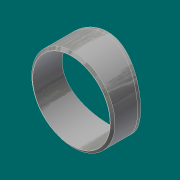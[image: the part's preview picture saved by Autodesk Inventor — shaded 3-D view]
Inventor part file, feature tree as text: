
AUTODESK INVENTOR PART (.ipt)
format: ipt  version: 2017.3 (Build 213257000, 257)  size: 175,616 bytes
history: native  units: in
note: dims shown in document units (in); Inventor stores cm internally (conversion verified against a paired STEP export)
features: extrude x5, other x5, sketch x3, split x3, chamfer x1, loft x1
ambient origin geometry x8: Origin, YZ Plane, XZ Plane, XY Plane, X Axis, Y Axis, Z Axis, Center Point
bodies: Solid1 (feature_tree)
feature tree (18):
  extrude  "Extrusion1"  Depth=13.0in
  sketch  "Sketch2"  dims[d2=22.0106in d3=0.0in d4=34.125in d5=20.1562in d6=0.0in]
  extrude  "Extrusion2"  Depth=34.125in
  split  "Split1"
  split  "Split2"
  chamfer  "Chamfer1"  Distance=20.1562in
  split  "Split3"
  loft  "Loft1"
  sketch  "Sketch1"  dims[d0=14.0in d1=13.0in]
  other  "Srf1"
  other  "Srf2"
  sketch  "Sketch3"  dims[d7=34.75in d8=35.75in d9=0.0in d10=0.0in d11=0.0in d12=0.0in d13=0.4375in d14=0.125in d15=0.2577in d16=13.125in d17=1.0in d18=0.0in d19=0.0in d20=90.0deg d21=0.0in d22=90.0deg]
  other  "Srf3"
  other  "Edges1"
  other  "Edges2"
  extrude  "ExtrusionSrf1"  TaperAngle=0.0deg  [1 undecoded]
  extrude  "ExtrusionSrf2"  TaperAngle=0.0deg  [1 undecoded]
  extrude  "ExtrusionSrf3"  Depth=0.4375in
note: 2 required parameter values undecoded (feature->parameter linkage not recoverable at this tier; creation-order binding heuristic only, values carry confidence <= 0.55)
